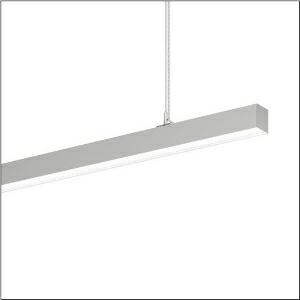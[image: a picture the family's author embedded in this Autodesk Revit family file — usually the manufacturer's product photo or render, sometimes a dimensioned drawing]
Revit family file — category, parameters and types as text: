
# Revit family: silica_21_51mx30db45sb
name_source: partatom
category: Lighting Fixtures
units: mm (PartAtom-declared; Revit-internal decimal feet)

## family parameters
Cut with Voids When Loaded = No
Host = Face
Light Source = No
Part Type = Normal
Room Calculation Point = No
Round Connector Dimension = Use Diameter
Shared = No

## types (1)
- --- (1 x LED, 5260 lm, 32 W, 4000K)
    Apparent Load = 32 VA
    CIE Flux Codes = 47 79 96 57 100
    Color Rendering = 80
    Color Temperature = 4000K
    Default Elevation = 1800 mm
    Description = Silica 21, office luminaire, primary optical cover: cover, of PMMA, opal, light emission: direct/indirect distribution, primary light characteristic: symmetric, installation type: suspended mounting, LED, rated luminous flux: 5.260lm, luminous efficacy: 164lm/W, light colour: 840, colour temperature: 4000K, control gear: DALI 2, with terminal, 3+2-pole, max. 2.5mm², mains connection: 220..240V, AC, 50/60Hz, rated input power: 32W, luminaire housing, of aluminium, metallic grey (RAL 9006), length: 1.504mm, width: 53mm, height: 53mm, protection rating (complete): IP20, insulation class (complete): insulation class I (protective earthing), certification: CE, permissible operating ambient temperature: 0..+35°C, standard: EN 50419, packaging unit: 1 piece
    Height = 53 mm
    Lamp = 1 x LED
    Lamp Light Flux = 5260 lm
    Lamp Power = 32 W
    Lamp count = 1
    Length = 1504 mm
    Luminous efficacy = 164 lm/W
    Manufacturer = Siteco
    ModVariant = No
    Model = 51MX30DB45SB
    Mounting Place = Ceiling
    Mounting Type = Pendant
    Number of Poles = 1
    OnlyDefault = Yes
    Power Factor = 1
    Product Name = Silica 21
    Product group = office luminaire | ceiling pendant
    ProductGroupID = 903
    Protection Class = Protection class I
    Protection Degree = IP 20
    RLX_Detail_Level = 1
    RLX_Emergency_Light_Flux = 0 lm
    RLX_Emergency_Type = 0
    RLX_Emergency_Type_DB = No
    RlxData = <blob elided: 23329 chars, md5=be0fc237>
    Socket = socket
    Standby Power = 0 W
    System Light Flux = 5260 lm
    System Power = 32 W
    Type Comments = factory setting: luminous flux: 100 % | dim-lin: 254 | 218 mA
    Type Image = l_1335864.jpg
    URL = http://relux.com
    VarID = @adj_117103
    Voltage = 0 V
    Weight = 0.00 kg
    Width = 53 mm

## geometry (parser evidence)
native form markers: Blend x4, Sweep x12
no freeform markers — native parametric forms only
